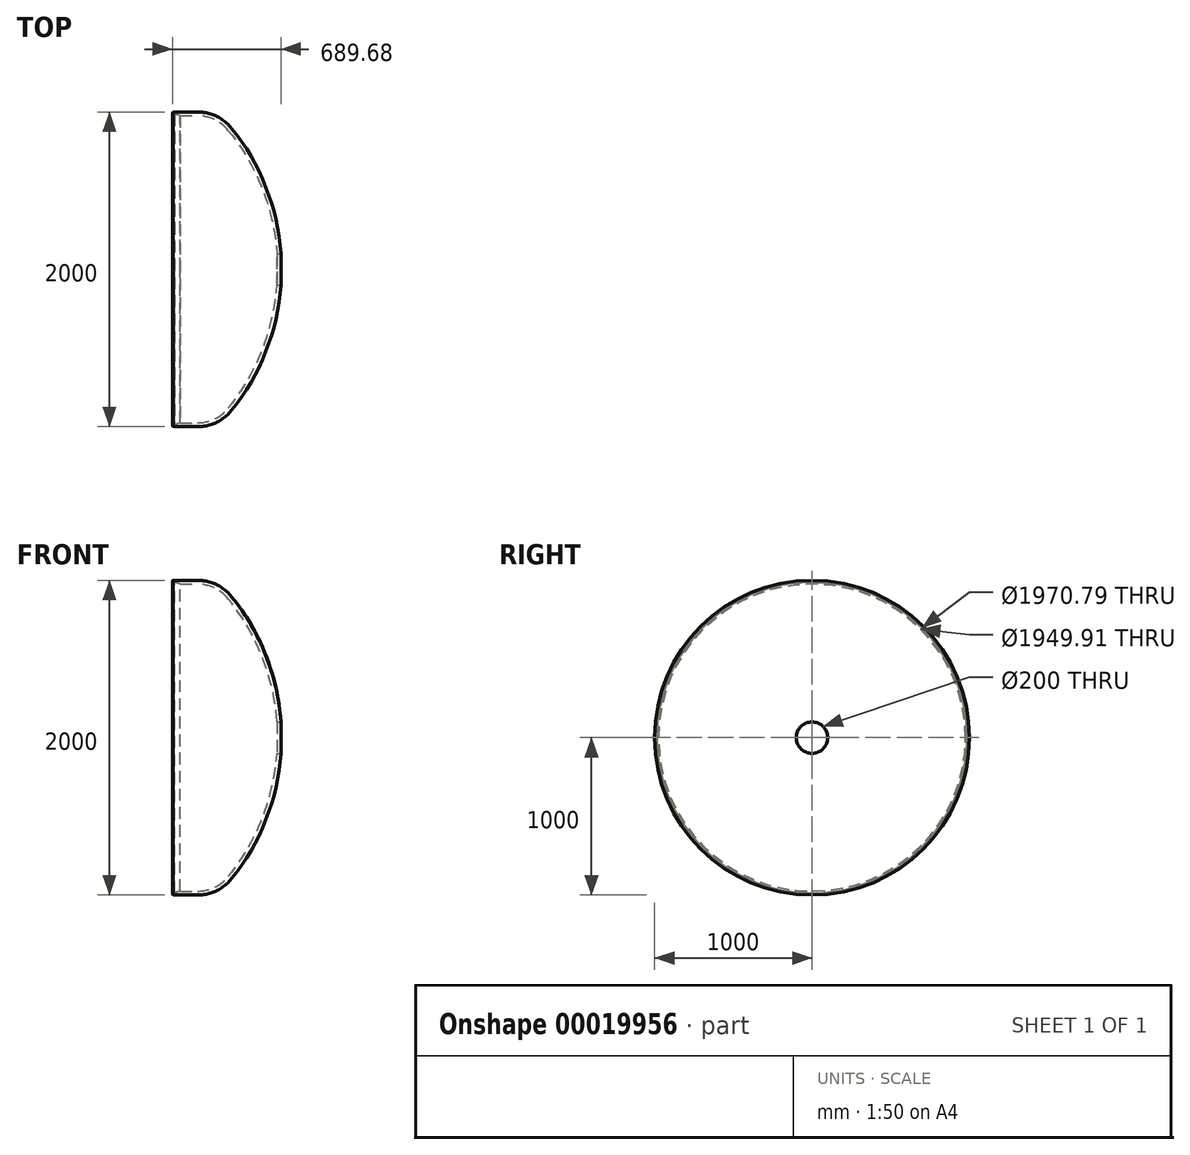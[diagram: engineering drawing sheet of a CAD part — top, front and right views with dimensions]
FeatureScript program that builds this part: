
annotation { "Feature Type Name" : "Feature", "Feature Type Description" : "" }
export const myFeature = defineFeature(function(context is Context, id is Id, definition is map)
    precondition{}
    {
        {
            var Q0;
            Q0=qCreatedBy(makeId("Front.planeOp"),FACE);
            var sketch = newSketch(context, id + "F0", { "sketchPlane" : qUnion([Q0])});
            skLineSegment(sketch, "E0", {"start": v(731.8, 1000) * mm, "end": v(1015.2, 1000) * mm});
            skArc(sketch, "E1.trimOffspring", {"start": v(1400, 0) * mm, "mid": v(1297.4, 526.02) * mm, "end": v(1004.68, 974.95) * mm});
            skArc(sketch, "E2.trimOffspring", {"start": v(1425, 0) * mm, "mid": v(1318.58, 540.36) * mm, "end": v(1015.2, 1000) * mm});
            skLineSegment(sketch, "E3", {"start": v(1425, 0) * mm, "end": v(895, 0) * mm, "construction": true});
            skLineSegment(sketch, "E4", {"start": v(1004.68, 974.95) * mm, "end": v(781.77, 974.95) * mm});
            skLineSegment(sketch, "E5", {"start": v(895, 0) * mm, "end": v(895, 974.95) * mm, "construction": true});
            skLineSegment(sketch, "E6", {"start": v(895, 0) * mm, "end": v(895, -975) * mm, "construction": true});
            skLineSegment(sketch, "E7", {"start": v(731.8, 1000) * mm, "end": v(731.8, 974.95) * mm, "construction": true});
            skPoint(sketch, "E8.trimOffspring.end.orphan", {"position": v(731.8, -1000) * mm});
            skPoint(sketch, "E8.trimOffspring.start.orphan", {"position": v(731.8, -974.95) * mm});
            skLineSegment(sketch, "E9", {"start": v(1400, 0) * mm, "end": v(1425, 0) * mm});
            skLineSegment(sketch, "E10", {"start": v(731.8, 1000) * mm, "end": v(731.8, 985.4) * mm});
            skLineSegment(sketch, "E11", {"start": v(731.8, 985.4) * mm, "end": v(745.58, 985.4) * mm});
            skLineSegment(sketch, "E12", {"start": v(781.77, 974.95) * mm, "end": v(745.58, 985.4) * mm});
            skSolve(sketch);
        }
        {
            var Q0;
            Q0=makeQuery(id+"F0.imprint","IMPRINT",FACE,{"disambiguationData":[TD([[makeQuery(id+"F0.imprint","IMPRINT",EDGE,{"derivedFrom":sQuery(id+"F0.wireOp",EDGE,"E0")}),-1.0]])]});
            var Q1;
            Q1=sQuery(id+"F0.wireOp",EDGE,"E3");
            revolve(context, id + "F1", {"entities" : qUnion([Q0]), "axis" : qUnion([Q1]), "revolveType" : RevolveType.FULL});
        }
        {
            var Q0;
            Q0=makeQuery(id+"F1.opRevolve","SWEPT_EDGE",EDGE,{"disambiguationData":[OSD([sQuery(id+"F0.wireOp",EDGE,"E1.trimOffspring"),sQuery(id+"F0.wireOp",EDGE,"E4")])]});
            fillet(context, id + "F2", {"entities" : qUnion([Q0]), "radius" : 250 * mm, "tangentPropagation" : true, "allowEdgeOverflow" : false});
        }
        {
            var Q0;
            Q0=makeQuery(id+"F1.opRevolve","SWEPT_EDGE",EDGE,{"disambiguationData":[OSD([sQuery(id+"F0.wireOp",EDGE,"E0"),sQuery(id+"F0.wireOp",EDGE,"E2.trimOffspring")])]});
            fillet(context, id + "F3", {"entities" : qUnion([Q0]), "radius" : 275 * mm, "tangentPropagation" : true, "allowEdgeOverflow" : false});
        }
        {
            var Q0;
            Q0=makeQuery(id+"F1.opRevolve","SWEPT_EDGE",EDGE,{"disambiguationData":[OSD([sQuery(id+"F0.wireOp",EDGE,"E0"),sQuery(id+"F0.wireOp",EDGE,"E10")])]});
            var Q1;
            Q1=makeQuery(id+"F1.opRevolve","SWEPT_EDGE",EDGE,{"disambiguationData":[OSD([sQuery(id+"F0.wireOp",EDGE,"E10"),sQuery(id+"F0.wireOp",EDGE,"E11")])]});
            chamfer(context, id + "F4", {"entities" : qUnion([Q0, Q1]), "width" : 5 * mm, "tangentPropagation" : true});
        }
        {
            var Q0;
            Q0=qCreatedBy(makeId("Right.planeOp"),FACE);
            cPlane(context, id + "F5", {"entities" : qUnion([Q0]), "cplaneType" : CPlaneType.OFFSET, "offset" : 1425 * mm, "width" : 150 * mm, "height" : 150 * mm});
        }
        {
            var Q0;
            Q0=qCreatedBy(id+"F5.planeOp",FACE);
            var sketch = newSketch(context, id + "F6", { "sketchPlane" : qUnion([Q0])});
            skPoint(sketch, "E13", {"position": v(0, 0) * mm});
            skSolve(sketch);
        }
        {
            var Q0;
            Q0=sQuery(id+"F6.wireOp",VERTEX,"E13");
            var Q1;
            Q1=makeQuery(id+"F1.opRevolve","SWEPT_BODY",BODY,{"disambiguationData":[OSD([sQuery(id+"F0.wireOp",EDGE,"E0"),sQuery(id+"F0.wireOp",EDGE,"E1.trimOffspring"),sQuery(id+"F0.wireOp",EDGE,"E2.trimOffspring"),sQuery(id+"F0.wireOp",EDGE,"E4"),sQuery(id+"F0.wireOp",EDGE,"E9"),sQuery(id+"F0.wireOp",EDGE,"E10"),sQuery(id+"F0.wireOp",EDGE,"E11"),sQuery(id+"F0.wireOp",EDGE,"E12")])]});
            hole(context, id + "F7", {"style" : HoleStyle.SIMPLE, "holeDiameter" : 200 * mm, "endStyle" : HoleEndStyle.THROUGH, "locations" : qUnion([Q0]), "scope" : qUnion([Q1])});
        }
    });
